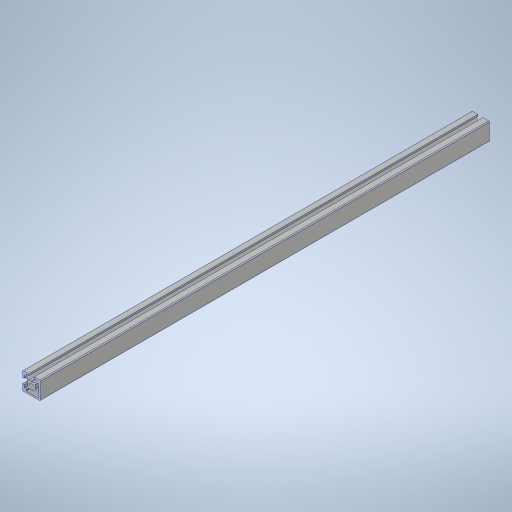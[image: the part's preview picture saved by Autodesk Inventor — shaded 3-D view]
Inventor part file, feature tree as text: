
AUTODESK INVENTOR PART (.ipt)
format: ipt  version: 2024 (Build 280153000, 153)  size: 368,640 bytes
history: native  units: mm
features: other x7, thread x2, sketch x2, extrude x1, hole x1
ambient origin geometry x8: Origin, YZ Plane, XZ Plane, XY Plane, X Axis, Y Axis, Z Axis, Center Point
bodies: Solid1 (feature_tree)
feature tree (13):
  extrude  "Extrusion1"  TaperAngle=0.0deg  [1 undecoded]
  hole  "Hole1"  [1 undecoded]
  other  "C1_XY"
  other  "C1_YZ"
  other  "C1_ZX"
  other  "C1_X"
  other  "C1_Y"
  other  "C1_Z"
  other  "C1_Center"
  thread  "Thread1"  [1 undecoded]
  thread  "Thread2"  [1 undecoded]
  sketch  "Sketch_64"  dims[d2=4.2mm d3=6.0mm d4=4.0mm d5=2.0mm d6=90.0deg d7=680.0mm d8=0.0mm d9=0.0mm d10=10.0mm d11=0.0mm d12=10.0mm d13=0.0mm]
  sketch  "Sketch2"  dims[d0=500.0mm d1=0.0mm]
note: 4 required parameter values undecoded (feature->parameter linkage not recoverable at this tier; creation-order binding heuristic only, values carry confidence <= 0.55)
